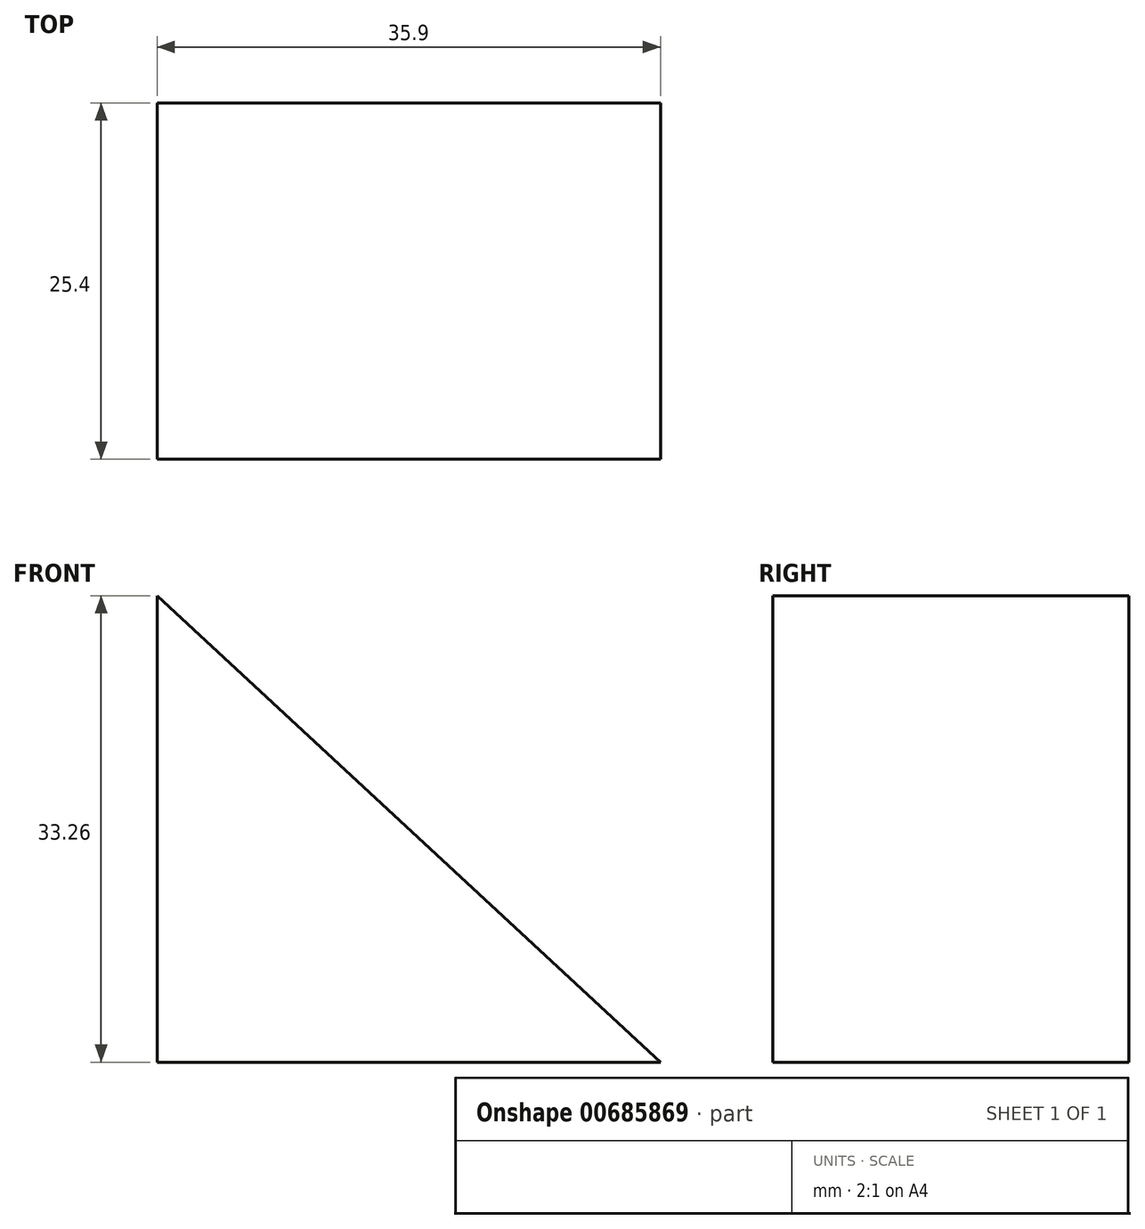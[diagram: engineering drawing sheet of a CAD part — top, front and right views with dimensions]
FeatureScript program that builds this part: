
annotation { "Feature Type Name" : "Feature", "Feature Type Description" : "" }
export const myFeature = defineFeature(function(context is Context, id is Id, definition is map)
    precondition{}
    {
        {
            var Q0;
            Q0=qCreatedBy(makeId("Front.planeOp"),FACE);
            var sketch = newSketch(context, id + "F0", { "sketchPlane" : qUnion([Q0])});
            skLineSegment(sketch, "E0", {"start": v(0, 0) * mm, "end": v(35.9, 0) * mm});
            skLineSegment(sketch, "E1", {"start": v(0, 0) * mm, "end": v(0, 33.26) * mm});
            skLineSegment(sketch, "E2", {"start": v(0, 33.26) * mm, "end": v(35.9, 0) * mm});
            skSolve(sketch);
        }
        {
            var Q0;
            Q0=makeQuery(id+"F0.imprint","IMPRINT",FACE,{"disambiguationData":[TD([[makeQuery(id+"F0.imprint","IMPRINT",EDGE,{"derivedFrom":sQuery(id+"F0.wireOp",EDGE,"E0")}),1.0]])]});
            extrude(context, id + "F1", {"entities" : qUnion([Q0]), "depth" : 25.4 * mm, "offsetDistance" : 25.4 * mm});
        }
    });
